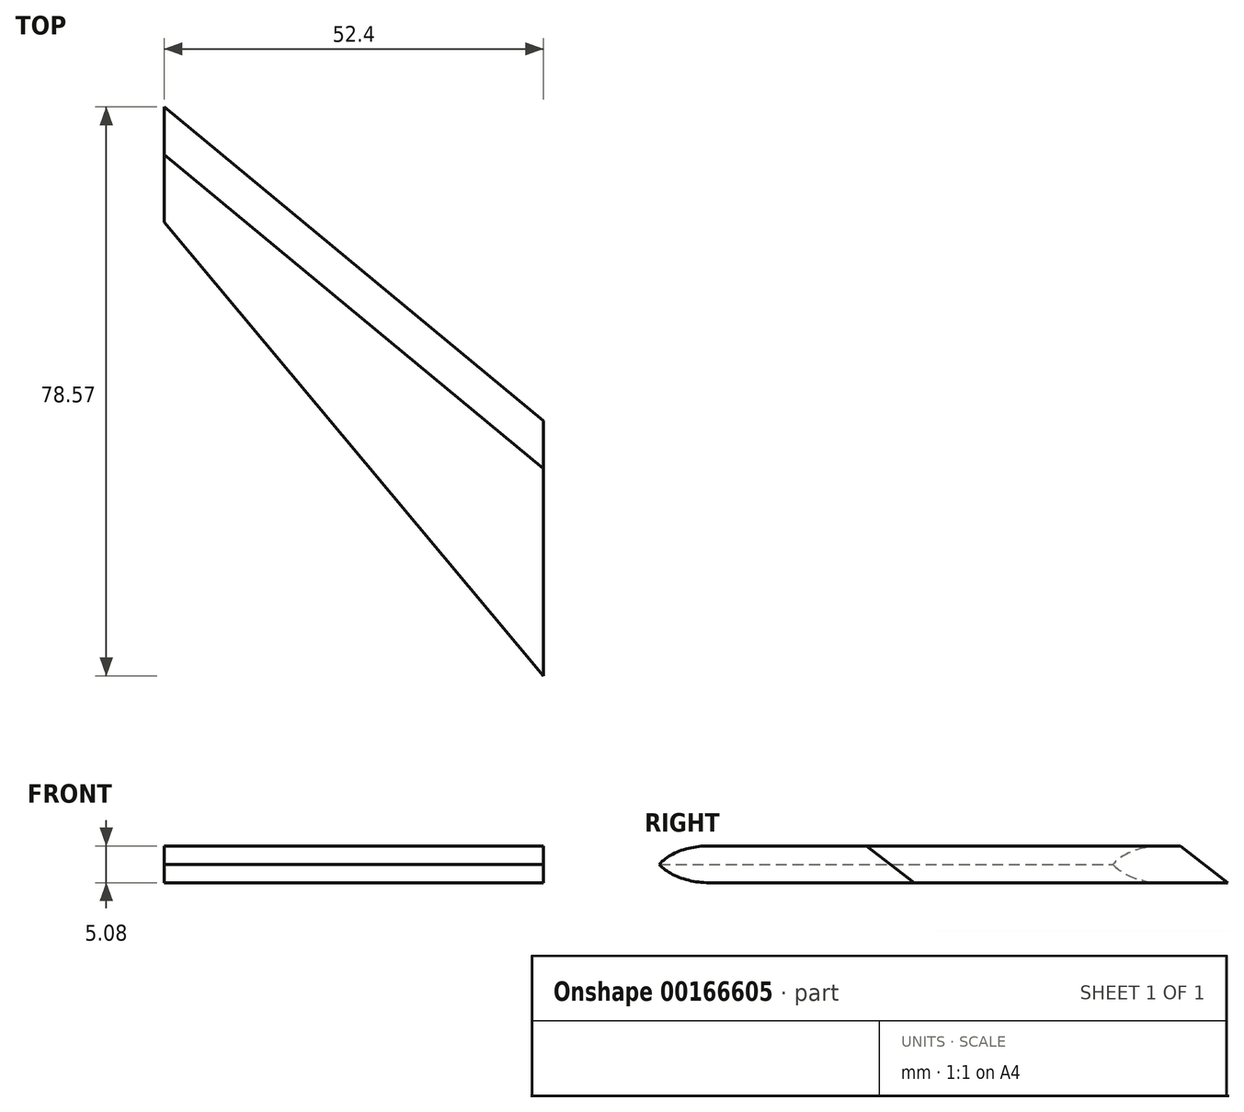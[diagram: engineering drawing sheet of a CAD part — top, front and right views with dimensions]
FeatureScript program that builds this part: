
annotation { "Feature Type Name" : "Feature", "Feature Type Description" : "" }
export const myFeature = defineFeature(function(context is Context, id is Id, definition is map)
    precondition{}
    {
        {
            var Q0;
            Q0=qCreatedBy(makeId("Top.planeOp"),FACE);
            var sketch = newSketch(context, id + "F0", { "sketchPlane" : qUnion([Q0])});
            skLineSegment(sketch, "E0", {"start": v(0, 0) * mm, "end": v(0, 36.28) * mm});
            skLineSegment(sketch, "E1", {"start": v(0, 36.28) * mm, "end": v(-52.4, 79.63) * mm});
            skLineSegment(sketch, "E2", {"start": v(-52.4, 79.63) * mm, "end": v(-52.4, 62.67) * mm});
            skLineSegment(sketch, "E3", {"start": v(-52.4, 62.67) * mm, "end": v(0, 0) * mm});
            skPoint(sketch, "E4.end.orphan", {"position": v(0, 79.63) * mm});
            skSolve(sketch);
        }
        {
            var Q0;
            Q0=makeQuery(id+"F0.imprint","IMPRINT",FACE,{"disambiguationData":[TD([[makeQuery(id+"F0.imprint","IMPRINT",EDGE,{"derivedFrom":sQuery(id+"F0.wireOp",EDGE,"E0")}),1.0]])]});
            extrude(context, id + "F1", {"entities" : qUnion([Q0]), "depth" : 5.08 * mm});
        }
        {
            var Q0;
            Q0=makeQuery(id+"F1.opExtrude","CAP_EDGE",EDGE,{"disambiguationData":[OSD([sQuery(id+"F0.wireOp",EDGE,"E3")])],"isStart":false});
            var Q1;
            Q1=makeQuery(id+"F1.opExtrude","CAP_EDGE",EDGE,{"disambiguationData":[OSD([sQuery(id+"F0.wireOp",EDGE,"E3")])],"isStart":true});
            fillet(context, id + "F2", {"entities" : qUnion([Q0, Q1]), "radius" : 5.08 * mm, "tangentPropagation" : true, "allowEdgeOverflow" : false});
        }
        {
            var Q0;
            Q0=makeQuery(id+"F1.opExtrude","CAP_EDGE",EDGE,{"disambiguationData":[OSD([sQuery(id+"F0.wireOp",EDGE,"E1")])],"isStart":false});
            chamfer(context, id + "F3", {"entities" : qUnion([Q0]), "width" : 5.08 * mm, "tangentPropagation" : true});
        }
    });
